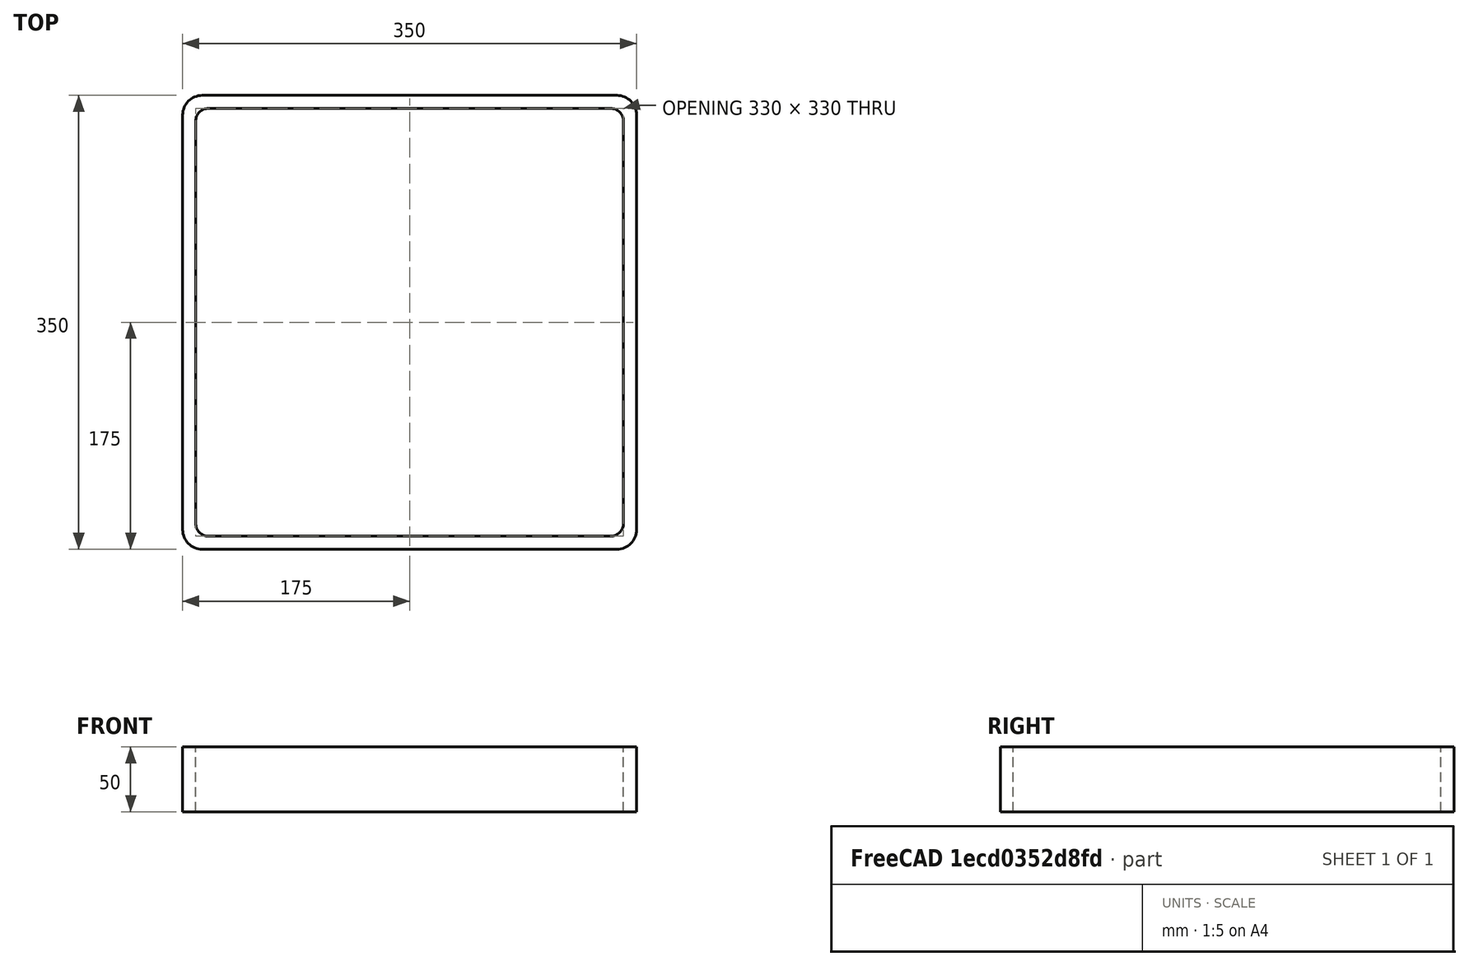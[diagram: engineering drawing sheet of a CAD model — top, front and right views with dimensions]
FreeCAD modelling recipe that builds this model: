
FCSTD DOCUMENT  (FreeCAD 0.15R4671 (Git))
Label: Square hollow section 350x350x10 EN10219 S235JRH
License: All rights reserved
LicenseURL: http://en.wikipedia.org/wiki/All_rights_reserved
objects: Sketcher::SketchObject×1, Part::Extrusion×1
note: 2 computed .brp shape members not serialized (recipe doc carries the construction recipe); baked Part::Feature solids carry a one-line shape summary decoded from their .brp

FEATURE [Sketcher::SketchObject] Sketch
  sketch-geometry (16):
    g0: LineSegment StartX=-155 StartY=165 StartZ=0 EndX=155 EndY=165 EndZ=0
    g1: LineSegment StartX=165 StartY=155 StartZ=0 EndX=165 EndY=-155 EndZ=0
    g2: LineSegment StartX=155 StartY=-165 StartZ=0 EndX=-155 EndY=-165 EndZ=0
    g3: LineSegment StartX=-165 StartY=-155 StartZ=0 EndX=-165 EndY=155 EndZ=0
    g4: LineSegment StartX=-160 StartY=175 StartZ=0 EndX=160 EndY=175 EndZ=0
    g5: LineSegment StartX=175 StartY=160 StartZ=0 EndX=175 EndY=-160 EndZ=0
    g6: LineSegment StartX=160 StartY=-175 StartZ=0 EndX=-160 EndY=-175 EndZ=0
    g7: LineSegment StartX=-175 StartY=-160 StartZ=0 EndX=-175 EndY=160 EndZ=0
    g8: ArcOfCircle CenterX=-155 CenterY=155 CenterZ=0 NormalX=0 NormalY=0 NormalZ=1 Radius=10 StartAngle=1.5708 EndAngle=3.14159
    g9: ArcOfCircle CenterX=155 CenterY=155 CenterZ=0 NormalX=0 NormalY=0 NormalZ=1 Radius=10 StartAngle=0 EndAngle=1.5708
    g10: ArcOfCircle CenterX=155 CenterY=-155 CenterZ=0 NormalX=0 NormalY=0 NormalZ=1 Radius=10 StartAngle=4.71239 EndAngle=6.28319
    g11: ArcOfCircle CenterX=-155 CenterY=-155 CenterZ=0 NormalX=0 NormalY=0 NormalZ=1 Radius=10 StartAngle=3.14159 EndAngle=4.71239
    g12: ArcOfCircle CenterX=160 CenterY=160 CenterZ=0 NormalX=0 NormalY=0 NormalZ=1 Radius=15 StartAngle=0 EndAngle=1.5708
    g13: ArcOfCircle CenterX=160 CenterY=-160 CenterZ=0 NormalX=0 NormalY=0 NormalZ=1 Radius=15 StartAngle=4.71239 EndAngle=6.28319
    g14: ArcOfCircle CenterX=-160 CenterY=-160 CenterZ=0 NormalX=0 NormalY=0 NormalZ=1 Radius=15 StartAngle=3.14159 EndAngle=4.71239
    g15: ArcOfCircle CenterX=-160 CenterY=160 CenterZ=0 NormalX=0 NormalY=0 NormalZ=1 Radius=15 StartAngle=1.5708 EndAngle=3.14159
  constraints (36):
    c: Horizontal(g2)
    c: Vertical(g3)
    c: Horizontal(g6)
    c: Vertical(g7)
    c: Tangent(g3,g8) = 1.5708
    c: Tangent(g0,g8) = 1.5708
    c: Tangent(g0,g9) = 1.5708
    c: Tangent(g1,g9) = 1.5708
    c: Tangent(g1,g10) = 1.5708
    c: Tangent(g2,g10) = 1.5708
    c: Tangent(g2,g11) = 1.5708
    c: Tangent(g3,g11) = 1.5708
    c: Tangent(g4,g12) = 1.5708
    c: Tangent(g5,g12) = 1.5708
    c: Tangent(g5,g13) = 1.5708
    c: Tangent(g6,g13) = 1.5708
    c: Tangent(g6,g14) = 1.5708
    c: Tangent(g7,g14) = 1.5708
    c: Tangent(g7,g15) = 1.5708
    c: Tangent(g4,g15) = 1.5708
    c: Equal(g9,g8)
    c: Equal(g9,g11)
    c: Equal(g9,g10)
    c: Equal(g12,g15)
    c: Equal(g12,g14)
    c: Equal(g12,g13)
    c: Symmetric(g4,g6,g-1)
    c: Symmetric(g7,g5,g-2)
    c: DistanceY(g4,g6) = -350
    c: DistanceX(g7,g5) = 350
    c: Symmetric(g3,g1,g-2)
    c: Symmetric(g0,g2,g-1)
    c: DistanceY(g0,g4) = 10
    c: DistanceX(g5,g1) = -10
    c: Radius(g9) = 10
    c: Radius(g12) = 15
FEATURE [Part::Extrusion] Extrude  label="Square hollow section 350x350x10 EN10219 S235JRH"
  Base = -> Sketch
  Dir = (0,0,50)
  Solid = true
